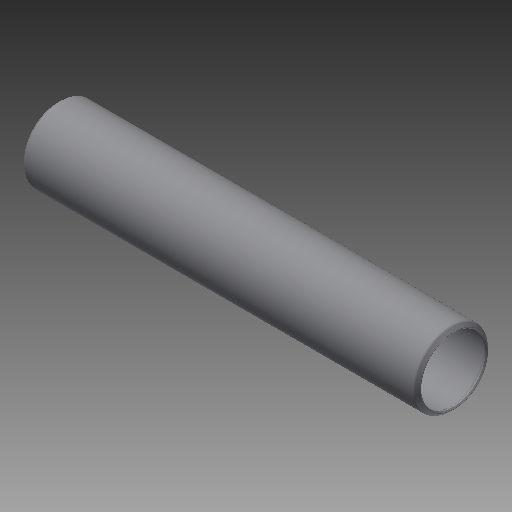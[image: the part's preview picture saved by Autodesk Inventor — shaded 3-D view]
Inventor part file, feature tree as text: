
AUTODESK INVENTOR PART (.ipt)
format: ipt  version: 2019 (Build 230136000, 136)  size: 155,136 bytes
history: native  units: in
note: dims shown in document units (in); Inventor stores cm internally (conversion verified against a paired STEP export)
features: other x42, revolve x1, sketch x1
ambient origin geometry x8: Origin, YZ Plane, XZ Plane, XY Plane, X Axis, Y Axis, Z Axis, Center Point
bodies: Solid1 (feature_tree)
feature tree (44):
  revolve  "Revolution1"  [1 undecoded]
  other  "cp1_XY"
  other  "cp1_YZ"
  other  "cp1_ZX"
  other  "cp1_X"
  other  "cp1_Y"
  other  "cp1_Z"
  other  "cp1_Center"
  other  "cp2_XY"
  other  "cp2_YZ"
  other  "cp2_ZX"
  other  "cp2_X"
  other  "cp2_Y"
  other  "cp2_Z"
  other  "cp2_Center"
  other  "cp3_XY"
  other  "cp3_YZ"
  other  "cp3_ZX"
  other  "cp3_X"
  other  "cp3_Y"
  other  "cp3_Z"
  other  "cp3_Center"
  other  "cp4_XY"
  other  "cp4_YZ"
  other  "cp4_ZX"
  other  "cp4_X"
  other  "cp4_Y"
  other  "cp4_Z"
  other  "cp4_Center"
  other  "tube_front_XY"
  other  "tube_front_YZ"
  other  "tube_front_ZX"
  other  "tube_front_X"
  other  "tube_front_Y"
  other  "tube_front_Z"
  other  "tube_front_Center"
  other  "tube_rear_XY"
  other  "tube_rear_YZ"
  other  "tube_rear_ZX"
  other  "tube_rear_X"
  other  "tube_rear_Y"
  other  "tube_rear_Z"
  other  "tube_rear_Center"
  sketch  "Sketch_1"  dims[d0=360.0deg]
note: 1 required parameter value undecoded (feature->parameter linkage not recoverable at this tier; creation-order binding heuristic only, values carry confidence <= 0.55)
